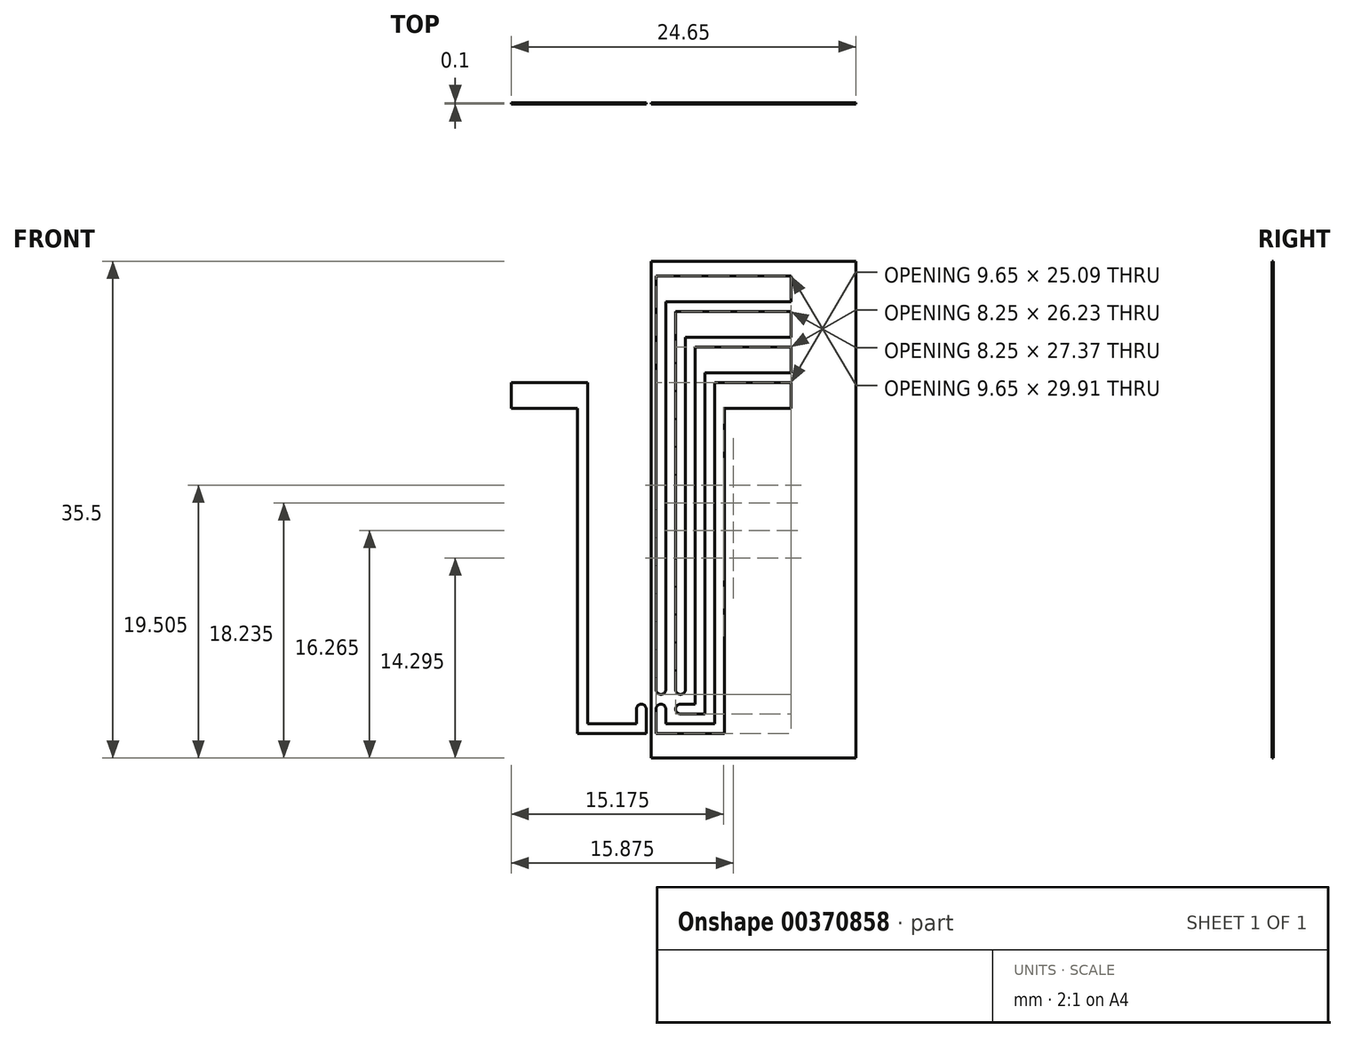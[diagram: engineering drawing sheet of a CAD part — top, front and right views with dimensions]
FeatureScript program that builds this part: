
annotation { "Feature Type Name" : "Feature", "Feature Type Description" : "" }
export const myFeature = defineFeature(function(context is Context, id is Id, definition is map)
    precondition{}
    {
        {
            var Q0;
            Q0=qCreatedBy(makeId("Front.planeOp"),FACE);
            var sketch = newSketch(context, id + "F0", { "sketchPlane" : qUnion([Q0])});
            skArc(sketch, "E0", {"start": v(1.05, 3.5) * mm, "mid": v(0.7, 3.85) * mm, "end": v(0.35, 3.5) * mm});
            skArc(sketch, "E1.0.1.0", {"start": v(0.35, 4.9) * mm, "mid": v(0.7, 4.55) * mm, "end": v(1.05, 4.9) * mm});
            skArc(sketch, "E1.1.0.0", {"start": v(2.1, 3.85) * mm, "mid": v(1.75, 3.5) * mm, "end": v(2.1, 3.15) * mm});
            skArc(sketch, "E1.1.1.0", {"start": v(1.75, 4.9) * mm, "mid": v(2.1, 4.55) * mm, "end": v(2.45, 4.9) * mm});
            skLineSegment(sketch, "E1.direction1", {"start": v(1.05, 3.5) * mm, "end": v(1.75, 3.5) * mm, "construction": true});
            skLineSegment(sketch, "E1.direction2", {"start": v(0.7, 3.5) * mm, "end": v(0.7, 4.9) * mm, "construction": true});
            skLineSegment(sketch, "E2.left", {"start": v(1.75, 4.9) * mm, "end": v(1.75, 30.08) * mm});
            skLineSegment(sketch, "E2.right", {"start": v(2.45, 4.9) * mm, "end": v(2.45, 30.08) * mm});
            skLineSegment(sketch, "E3.left", {"start": v(0.35, 3.5) * mm, "end": v(0.35, 2.45) * mm});
            skLineSegment(sketch, "E3.right", {"start": v(1.05, 3.5) * mm, "end": v(1.05, 2.45) * mm});
            skLineSegment(sketch, "E4.bottom", {"start": v(2.1, 3.85) * mm, "end": v(3.15, 3.85) * mm});
            skLineSegment(sketch, "E4.top", {"start": v(2.1, 3.15) * mm, "end": v(3.85, 3.15) * mm});
            skLineSegment(sketch, "E4.right", {"start": v(3.85, 3.85) * mm, "end": v(3.85, 3.15) * mm});
            skLineSegment(sketch, "E5.left", {"start": v(3.85, 3.85) * mm, "end": v(3.85, 27.54) * mm});
            skLineSegment(sketch, "E5.right", {"start": v(3.15, 3.85) * mm, "end": v(3.15, 27.54) * mm});
            skLineSegment(sketch, "E6.bottom", {"start": v(1.05, 2.45) * mm, "end": v(4.55, 2.45) * mm});
            skLineSegment(sketch, "E6.top", {"start": v(0.35, 1.75) * mm, "end": v(5.25, 1.75) * mm});
            skLineSegment(sketch, "E6.left", {"start": v(0.35, 2.45) * mm, "end": v(0.35, 1.75) * mm});
            skLineSegment(sketch, "E6.right", {"start": v(5.25, 2.45) * mm, "end": v(5.25, 1.75) * mm});
            skLineSegment(sketch, "E7.left", {"start": v(5.25, 2.45) * mm, "end": v(5.25, 25) * mm});
            skLineSegment(sketch, "E7.right", {"start": v(4.55, 2.45) * mm, "end": v(4.55, 25) * mm});
            skLineSegment(sketch, "E8.left", {"start": v(0.35, 4.9) * mm, "end": v(0.35, 32.62) * mm});
            skLineSegment(sketch, "E8.right", {"start": v(1.05, 4.9) * mm, "end": v(1.05, 32.62) * mm});
            skLineSegment(sketch, "E9.bottom", {"start": v(1.05, 32.62) * mm, "end": v(10, 32.62) * mm});
            skLineSegment(sketch, "E9.top", {"start": v(0.35, 34.46) * mm, "end": v(10, 34.46) * mm});
            skLineSegment(sketch, "E9.left", {"start": v(0.35, 32.62) * mm, "end": v(0.35, 34.46) * mm});
            skLineSegment(sketch, "E9.right", {"start": v(10, 32.62) * mm, "end": v(10, 34.46) * mm});
            skLineSegment(sketch, "E10.bottom", {"start": v(2.45, 30.08) * mm, "end": v(10, 30.08) * mm});
            skLineSegment(sketch, "E10.top", {"start": v(1.75, 31.92) * mm, "end": v(10, 31.92) * mm});
            skLineSegment(sketch, "E10.left", {"start": v(1.75, 30.08) * mm, "end": v(1.75, 31.92) * mm});
            skLineSegment(sketch, "E10.right", {"start": v(10, 30.08) * mm, "end": v(10, 31.92) * mm});
            skLineSegment(sketch, "E11.bottom", {"start": v(3.85, 27.54) * mm, "end": v(10, 27.54) * mm});
            skLineSegment(sketch, "E11.top", {"start": v(3.15, 29.38) * mm, "end": v(10, 29.38) * mm});
            skLineSegment(sketch, "E11.left", {"start": v(3.15, 27.54) * mm, "end": v(3.15, 29.38) * mm});
            skLineSegment(sketch, "E11.right", {"start": v(10, 27.54) * mm, "end": v(10, 29.38) * mm});
            skLineSegment(sketch, "E12.bottom", {"start": v(5.25, 25) * mm, "end": v(10, 25) * mm});
            skLineSegment(sketch, "E12.top", {"start": v(4.55, 26.84) * mm, "end": v(10, 26.84) * mm});
            skLineSegment(sketch, "E12.left", {"start": v(4.55, 25) * mm, "end": v(4.55, 26.84) * mm});
            skLineSegment(sketch, "E12.right", {"start": v(10, 25) * mm, "end": v(10, 26.84) * mm});
            skLineSegment(sketch, "E13", {"start": v(0, 0) * mm, "end": v(0, 11.53) * mm, "construction": true});
            skLineSegment(sketch, "E14", {"start": v(-6.2, 0) * mm, "end": v(8.89, 0) * mm, "construction": true});
            skLineSegment(sketch, "E15", {"start": v(10, 26.45) * mm, "end": v(10, -2.14) * mm, "construction": true});
            skArc(sketch, "E16.MirrorCS", {"start": v(-1.05, 3.5) * mm, "mid": v(-0.7, 3.85) * mm, "end": v(-0.35, 3.5) * mm});
            skArc(sketch, "E17.MirrorCS", {"start": v(-0.35, 4.9) * mm, "mid": v(-0.7, 4.55) * mm, "end": v(-1.05, 4.9) * mm});
            skLineSegment(sketch, "E18.MirrorCS", {"start": v(-1.05, 3.5) * mm, "end": v(-1.75, 3.5) * mm, "construction": true});
            skLineSegment(sketch, "E19.MirrorCS", {"start": v(-0.7, 3.5) * mm, "end": v(-0.7, 4.9) * mm, "construction": true});
            skArc(sketch, "E20.MirrorCS", {"start": v(-2.1, 3.85) * mm, "mid": v(-1.75, 3.5) * mm, "end": v(-2.1, 3.15) * mm});
            skArc(sketch, "E21.MirrorCS", {"start": v(-1.75, 4.9) * mm, "mid": v(-2.1, 4.55) * mm, "end": v(-2.45, 4.9) * mm});
            skLineSegment(sketch, "E22.MirrorCS", {"start": v(-5.25, 2.45) * mm, "end": v(-5.25, 1.75) * mm});
            skLineSegment(sketch, "E23.MirrorCS", {"start": v(-2.1, 3.15) * mm, "end": v(-3.85, 3.15) * mm});
            skLineSegment(sketch, "E24.MirrorCS", {"start": v(-3.85, 3.85) * mm, "end": v(-3.85, 3.15) * mm});
            skLineSegment(sketch, "E25.MirrorCS", {"start": v(-2.1, 3.85) * mm, "end": v(-3.15, 3.85) * mm});
            skLineSegment(sketch, "E26.MirrorCS", {"start": v(-1.05, 3.5) * mm, "end": v(-1.05, 2.45) * mm});
            skLineSegment(sketch, "E27.MirrorCS", {"start": v(-10, 25) * mm, "end": v(-10, 26.84) * mm});
            skLineSegment(sketch, "E28.MirrorCS", {"start": v(-0.35, 3.5) * mm, "end": v(-0.35, 2.45) * mm});
            skLineSegment(sketch, "E29.MirrorCS", {"start": v(-4.55, 25) * mm, "end": v(-4.55, 26.84) * mm});
            skLineSegment(sketch, "E30.MirrorCS", {"start": v(-0.35, 2.45) * mm, "end": v(-0.35, 1.75) * mm});
            skLineSegment(sketch, "E31.MirrorCS", {"start": v(-3.15, 29.38) * mm, "end": v(-10, 29.38) * mm});
            skLineSegment(sketch, "E32.MirrorCS", {"start": v(-1.05, 4.9) * mm, "end": v(-1.05, 32.62) * mm});
            skLineSegment(sketch, "E33.MirrorCS", {"start": v(-10, 32.62) * mm, "end": v(-10, 34.46) * mm});
            skLineSegment(sketch, "E34.MirrorCS", {"start": v(-1.05, 2.45) * mm, "end": v(-4.55, 2.45) * mm});
            skLineSegment(sketch, "E35.MirrorCS", {"start": v(-0.35, 4.9) * mm, "end": v(-0.35, 32.62) * mm});
            skLineSegment(sketch, "E36.MirrorCS", {"start": v(-0.35, 34.46) * mm, "end": v(-10, 34.46) * mm});
            skLineSegment(sketch, "E37.MirrorCS", {"start": v(-3.15, 27.54) * mm, "end": v(-3.15, 29.38) * mm});
            skLineSegment(sketch, "E38.MirrorCS", {"start": v(-10, 27.54) * mm, "end": v(-10, 29.38) * mm});
            skLineSegment(sketch, "E39.MirrorCS", {"start": v(-3.85, 27.54) * mm, "end": v(-10, 27.54) * mm});
            skLineSegment(sketch, "E40.MirrorCS", {"start": v(-2.45, 30.08) * mm, "end": v(-10, 30.08) * mm});
            skLineSegment(sketch, "E41.MirrorCS", {"start": v(-1.05, 32.62) * mm, "end": v(-10, 32.62) * mm});
            skLineSegment(sketch, "E42.MirrorCS", {"start": v(-1.75, 30.08) * mm, "end": v(-1.75, 31.92) * mm});
            skLineSegment(sketch, "E43.MirrorCS", {"start": v(-4.55, 26.84) * mm, "end": v(-10, 26.84) * mm});
            skLineSegment(sketch, "E44.MirrorCS", {"start": v(-0.35, 1.75) * mm, "end": v(-5.25, 1.75) * mm});
            skLineSegment(sketch, "E45.MirrorCS", {"start": v(-4.55, 2.45) * mm, "end": v(-4.55, 25) * mm});
            skLineSegment(sketch, "E46.MirrorCS", {"start": v(-3.85, 3.85) * mm, "end": v(-3.85, 27.54) * mm});
            skLineSegment(sketch, "E47.MirrorCS", {"start": v(-0.35, 32.62) * mm, "end": v(-0.35, 34.46) * mm});
            skLineSegment(sketch, "E48.MirrorCS", {"start": v(-5.25, 25) * mm, "end": v(-10, 25) * mm});
            skLineSegment(sketch, "E49.MirrorCS", {"start": v(-5.25, 2.45) * mm, "end": v(-5.25, 25) * mm});
            skLineSegment(sketch, "E50.MirrorCS", {"start": v(-10, 30.08) * mm, "end": v(-10, 31.92) * mm});
            skLineSegment(sketch, "E51.MirrorCS", {"start": v(-2.45, 4.9) * mm, "end": v(-2.45, 30.08) * mm});
            skLineSegment(sketch, "E52.MirrorCS", {"start": v(-1.75, 4.9) * mm, "end": v(-1.75, 30.08) * mm});
            skLineSegment(sketch, "E53.MirrorCS", {"start": v(-1.75, 31.92) * mm, "end": v(-10, 31.92) * mm});
            skLineSegment(sketch, "E54.MirrorCS", {"start": v(-3.15, 3.85) * mm, "end": v(-3.15, 27.54) * mm});
            skLineSegment(sketch, "E55.bottom", {"start": v(0, 0) * mm, "end": v(14.65, 0) * mm});
            skLineSegment(sketch, "E55.top", {"start": v(0, 35.5) * mm, "end": v(14.65, 35.5) * mm});
            skLineSegment(sketch, "E55.left", {"start": v(0, 0) * mm, "end": v(0, 35.5) * mm});
            skLineSegment(sketch, "E55.right", {"start": v(14.65, 0) * mm, "end": v(14.65, 35.5) * mm});
            skLineSegment(sketch, "E56.MirrorCS", {"start": v(0, 0) * mm, "end": v(-14.65, 0) * mm});
            skLineSegment(sketch, "E57.MirrorCS", {"start": v(0, 35.5) * mm, "end": v(-14.65, 35.5) * mm});
            skLineSegment(sketch, "E58.MirrorCS", {"start": v(-14.65, 0) * mm, "end": v(-14.65, 35.5) * mm});
            skSolve(sketch);
        }
        {
            var Q0;
            Q0=makeQuery(id+"F0.imprint","IMPRINT",FACE,{"disambiguationData":[TD([[makeQuery(id+"F0.imprint","IMPRINT",EDGE,{"derivedFrom":sQuery(id+"F0.wireOp",EDGE,"E0")}),-1.0]])]});
            var Q1;
            Q1=makeQuery(id+"F0.imprint","IMPRINT",FACE,{"disambiguationData":[TD([[makeQuery(id+"F0.imprint","IMPRINT",EDGE,{"derivedFrom":sQuery(id+"F0.wireOp",EDGE,"E16.MirrorCS")}),1.0]])]});
            extrude(context, id + "F1", {"entities" : qUnion([Q0, Q1]), "oppositeDirection" : true, "depth" : 0.1 * mm});
        }
        {
            var Q0;
            Q0 = qSketchRegion(id + "F0", true);
            extrude(context, id + "F2", {"entities" : qUnion([Q0]), "operationType" : NewBodyOperationType.REMOVE, "depth" : 0.1 * mm});
        }
    });
